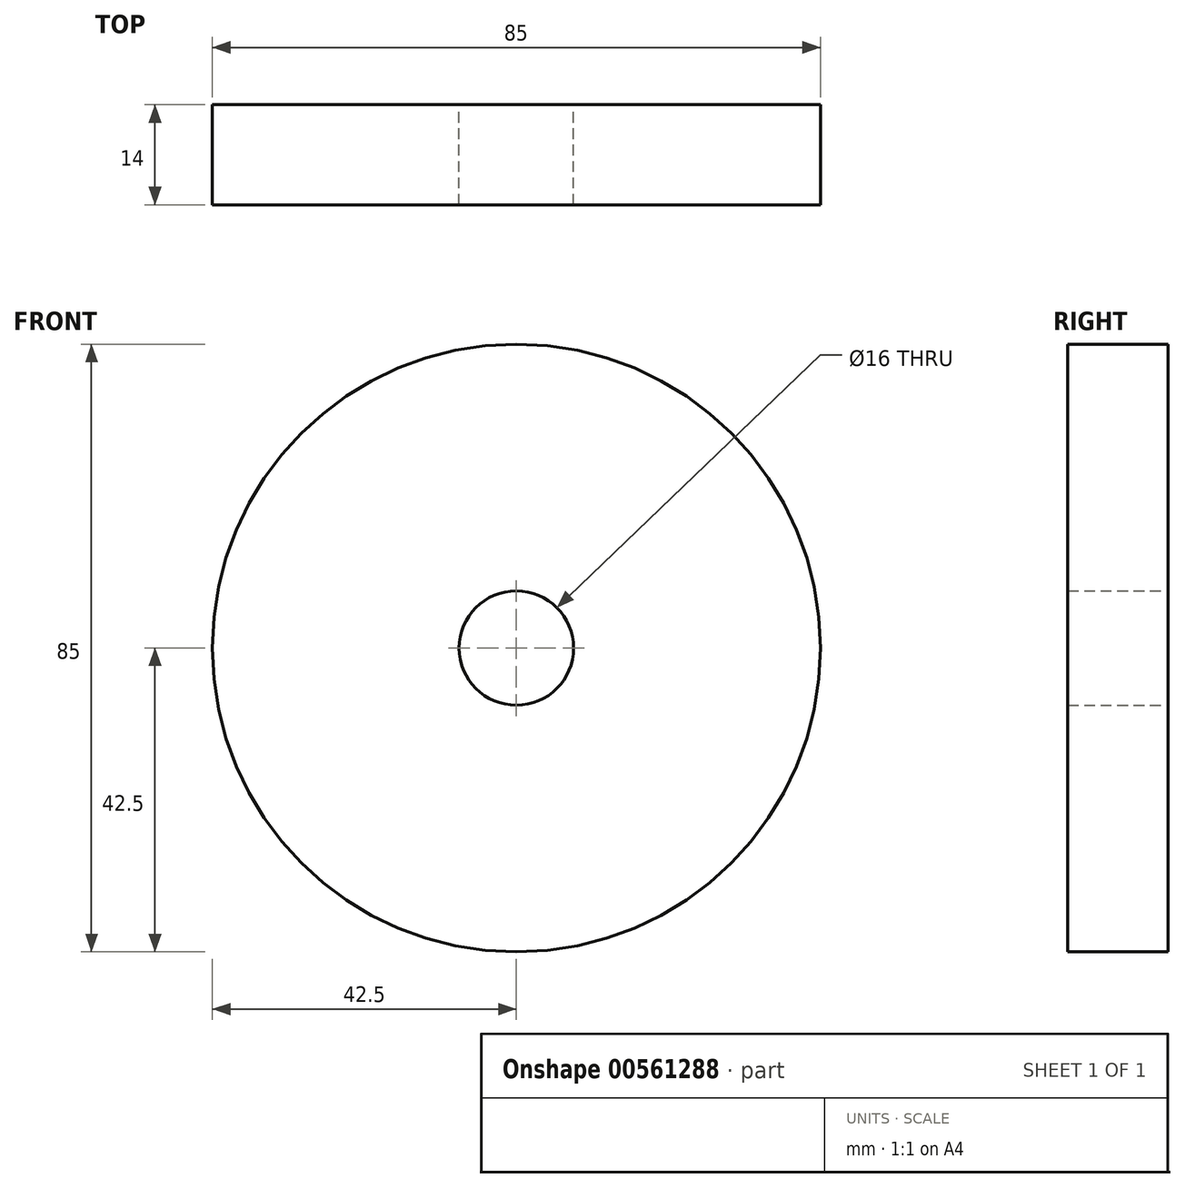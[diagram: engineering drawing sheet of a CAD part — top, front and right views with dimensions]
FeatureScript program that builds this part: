
annotation { "Feature Type Name" : "Feature", "Feature Type Description" : "" }
export const myFeature = defineFeature(function(context is Context, id is Id, definition is map)
    precondition{}
    {
        {
            var Q0;
            Q0=qCreatedBy(makeId("Front.planeOp"),FACE);
            var sketch = newSketch(context, id + "F0", { "sketchPlane" : qUnion([Q0])});
            skCircle(sketch, "E0", {"center": v(0, 0) * mm, "radius": 42.5 * mm});
            skCircle(sketch, "E1", {"center": v(0, 0) * mm, "radius": 8 * mm});
            skSolve(sketch);
        }
        {
            var Q0;
            Q0 = qSketchRegion(id + "F0", true);
            extrude(context, id + "F1", {"entities" : qUnion([Q0]), "depth" : 14 * mm, "offsetDistance" : 25 * mm});
        }
    });
